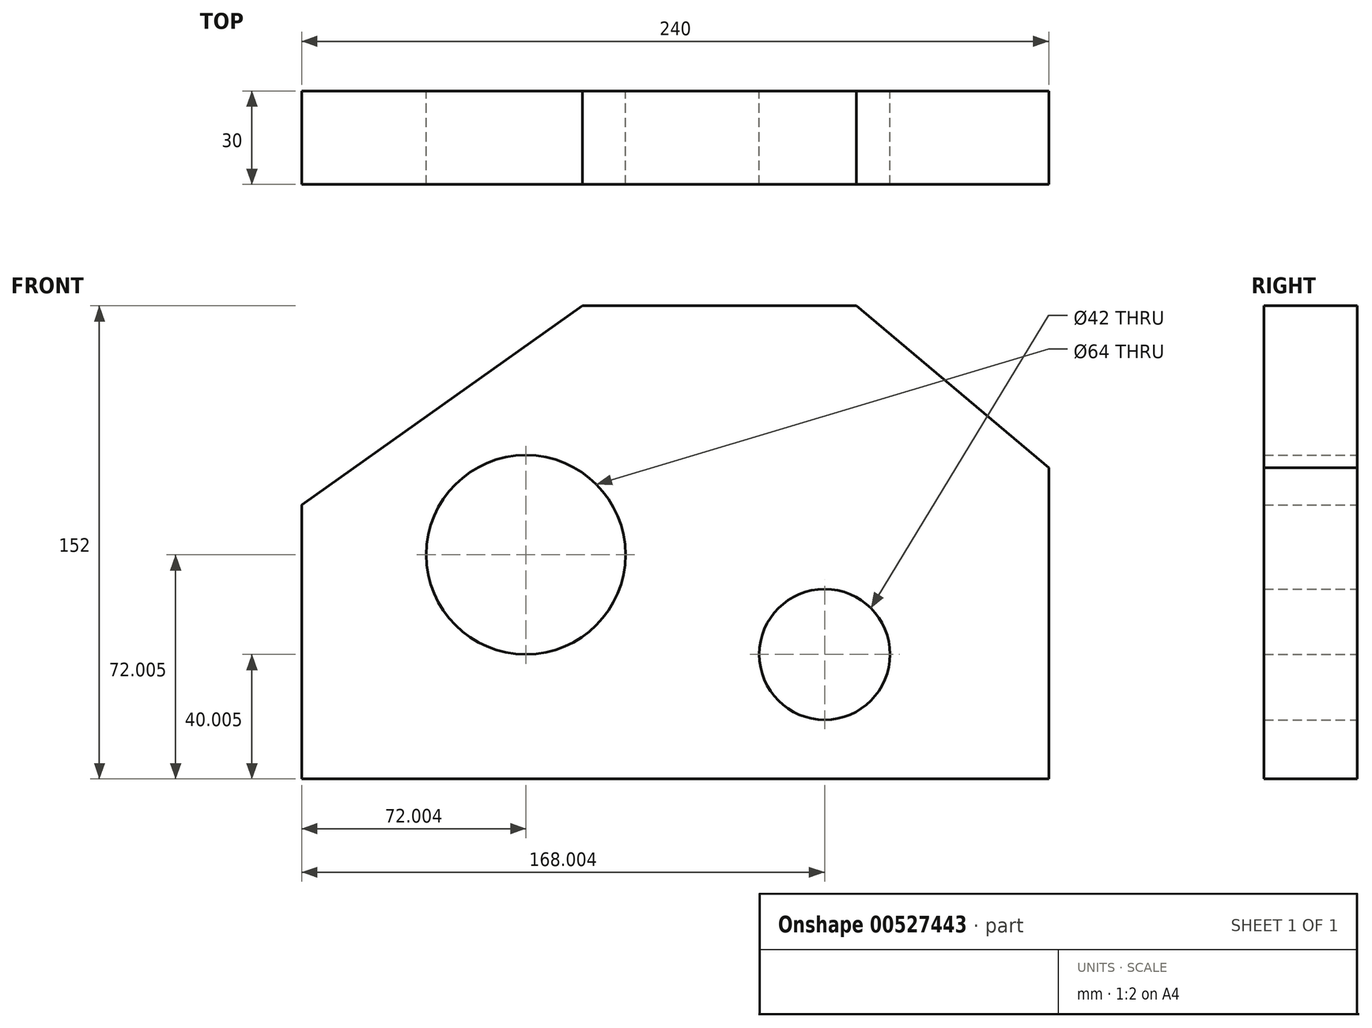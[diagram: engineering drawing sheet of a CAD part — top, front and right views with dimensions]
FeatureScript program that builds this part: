
annotation { "Feature Type Name" : "Feature", "Feature Type Description" : "" }
export const myFeature = defineFeature(function(context is Context, id is Id, definition is map)
    precondition{}
    {
        {
            var Q0;
            Q0=qCreatedBy(makeId("Front.planeOp"),FACE);
            var sketch = newSketch(context, id + "F0", { "sketchPlane" : qUnion([Q0])});
            skLineSegment(sketch, "E0", {"start": v(-178.15, 31.15) * mm, "end": v(-178.15, -56.85) * mm});
            skLineSegment(sketch, "E1", {"start": v(-178.15, 31.15) * mm, "end": v(-88, 95.15) * mm});
            skLineSegment(sketch, "E2", {"start": v(-88, 95.15) * mm, "end": v(0, 95.15) * mm});
            skLineSegment(sketch, "E3", {"start": v(0, 95.15) * mm, "end": v(61.85, 43.15) * mm});
            skLineSegment(sketch, "E4", {"start": v(61.85, 43.15) * mm, "end": v(61.85, -56.85) * mm});
            skLineSegment(sketch, "E5", {"start": v(-178.15, -56.85) * mm, "end": v(61.85, -56.85) * mm});
            skCircle(sketch, "E6", {"center": v(-10.15, -16.85) * mm, "radius": 21 * mm});
            skCircle(sketch, "E7", {"center": v(-106.15, 15.15) * mm, "radius": 32 * mm});
            skSolve(sketch);
        }
        {
            var Q0;
            Q0 = qSketchRegion(id + "F0", true);
            extrude(context, id + "F1", {"entities" : qUnion([Q0]), "depth" : 30 * mm, "offsetDistance" : 25 * mm});
        }
    });
